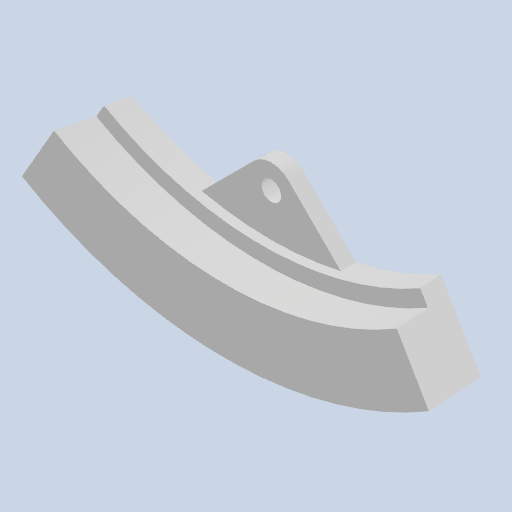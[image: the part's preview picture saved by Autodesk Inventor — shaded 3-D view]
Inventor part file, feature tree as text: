
AUTODESK INVENTOR PART (.ipt)
format: ipt  version: 2022 (Build 260153000, 153)  size: 169,984 bytes
history: native  units: mm
features: other x10, reference x10, extrude x4, sketch x3, projected_geometry x1
ambient origin geometry x8: Origin, YZ Plane, XZ Plane, XY Plane, X Axis, Y Axis, Z Axis, Center Point
bodies: Body1 (feature_tree)
feature tree (28):
  other  "Твердое тело1"
  extrude  "Выдавливание1"  Depth=10.0mm TaperAngle=0.0deg
  extrude  "Выдавливание4"  Depth=0.087266mm
  other  "НаклГрань1"
  other  "НаклГрань2"
  extrude  "Выдавливание5"  TaperAngle=60.0deg  [1 undecoded]
  extrude  "Выдавливание6"  TaperAngle=30.0deg  [1 undecoded]
  reference  "Ссылка1"
  reference  "Ссылка2"
  reference  "Ссылка3"
  reference  "Ссылка4"
  reference  "Ссылка5"
  reference  "Ссылка10"
  reference  "Ссылка11"
  sketch  "Эскиз4"
  reference  "Ссылка12"
  sketch  "Эскиз5"
  projected_geometry  "Спроецированная петля2"
  sketch  "Эскиз6"
  reference  "Ссылка13"
  reference  "Ссылка14"
  other  "<userpath>\Documents\Git\MZCAT_2024\MZCAT.iam"
  other  "MZCAT.iam"
  other  "vydacha_chertezh:1"
  other  "vydacha_backstenka:1"
  other  "magazine:1"
  other  "OCS-D008 B:1"
  other  "plan:1"
note: 2 required parameter values undecoded (feature->parameter linkage not recoverable at this tier; creation-order binding heuristic only, values carry confidence <= 0.55)
